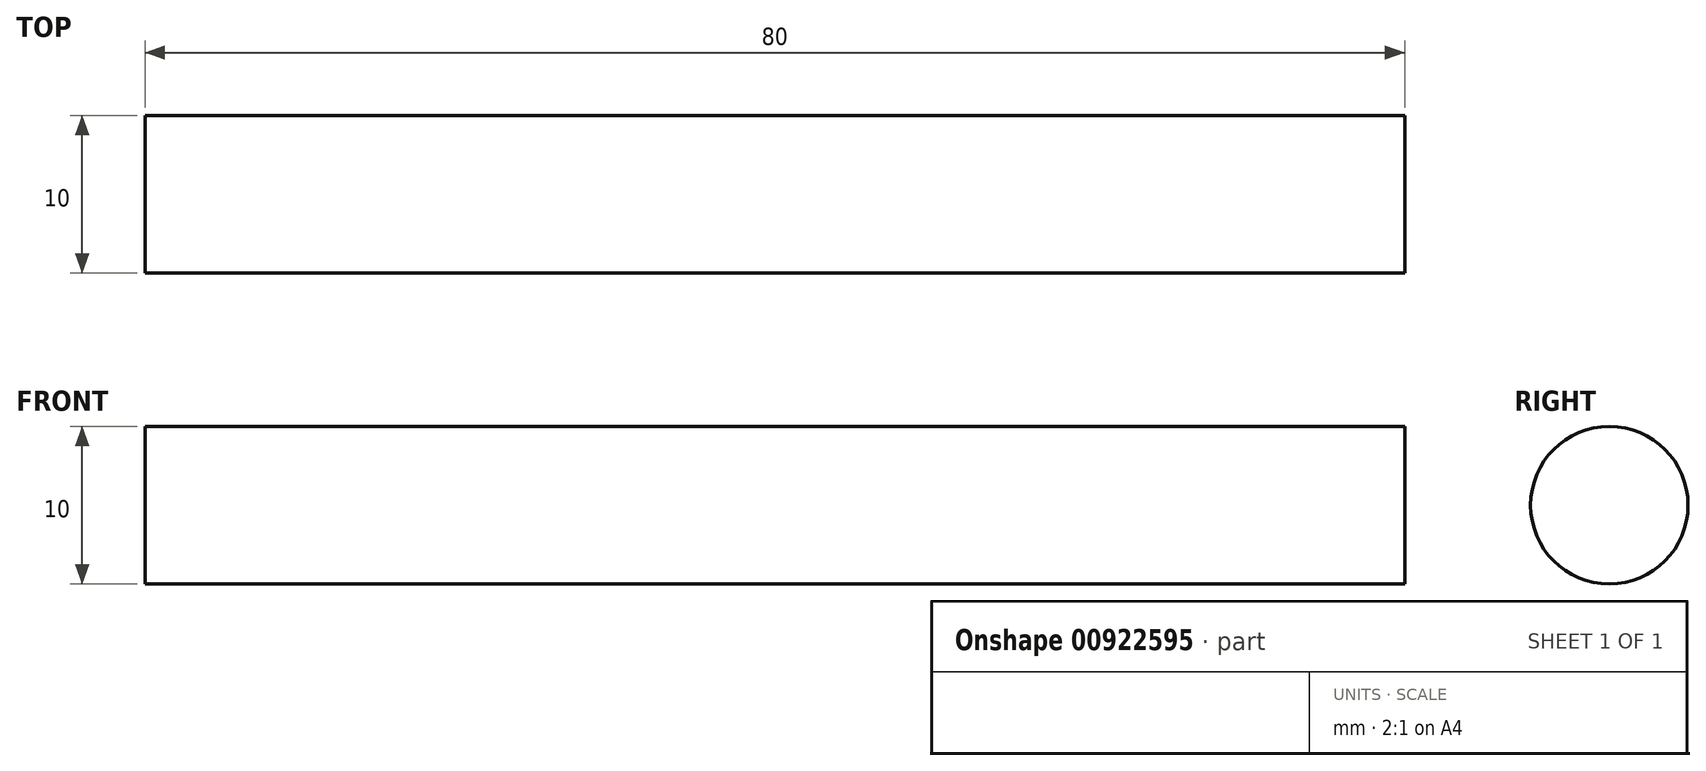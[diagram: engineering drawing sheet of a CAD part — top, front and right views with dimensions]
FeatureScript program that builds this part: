
annotation { "Feature Type Name" : "Feature", "Feature Type Description" : "" }
export const myFeature = defineFeature(function(context is Context, id is Id, definition is map)
    precondition{}
    {
        {
            var Q0;
            Q0=qCreatedBy(makeId("Right.planeOp"),FACE);
            var sketch = newSketch(context, id + "F0", { "sketchPlane" : qUnion([Q0])});
            skCircle(sketch, "E0", {"center": v(0, 0) * mm, "radius": 5 * mm});
            skSolve(sketch);
        }
        {
            var Q0;
            Q0 = qSketchRegion(id + "F0", true);
            extrude(context, id + "F1", {"entities" : qUnion([Q0]), "depth" : 80 * mm, "offsetDistance" : 25.4 * mm, "symmetric" : true});
        }
    });
